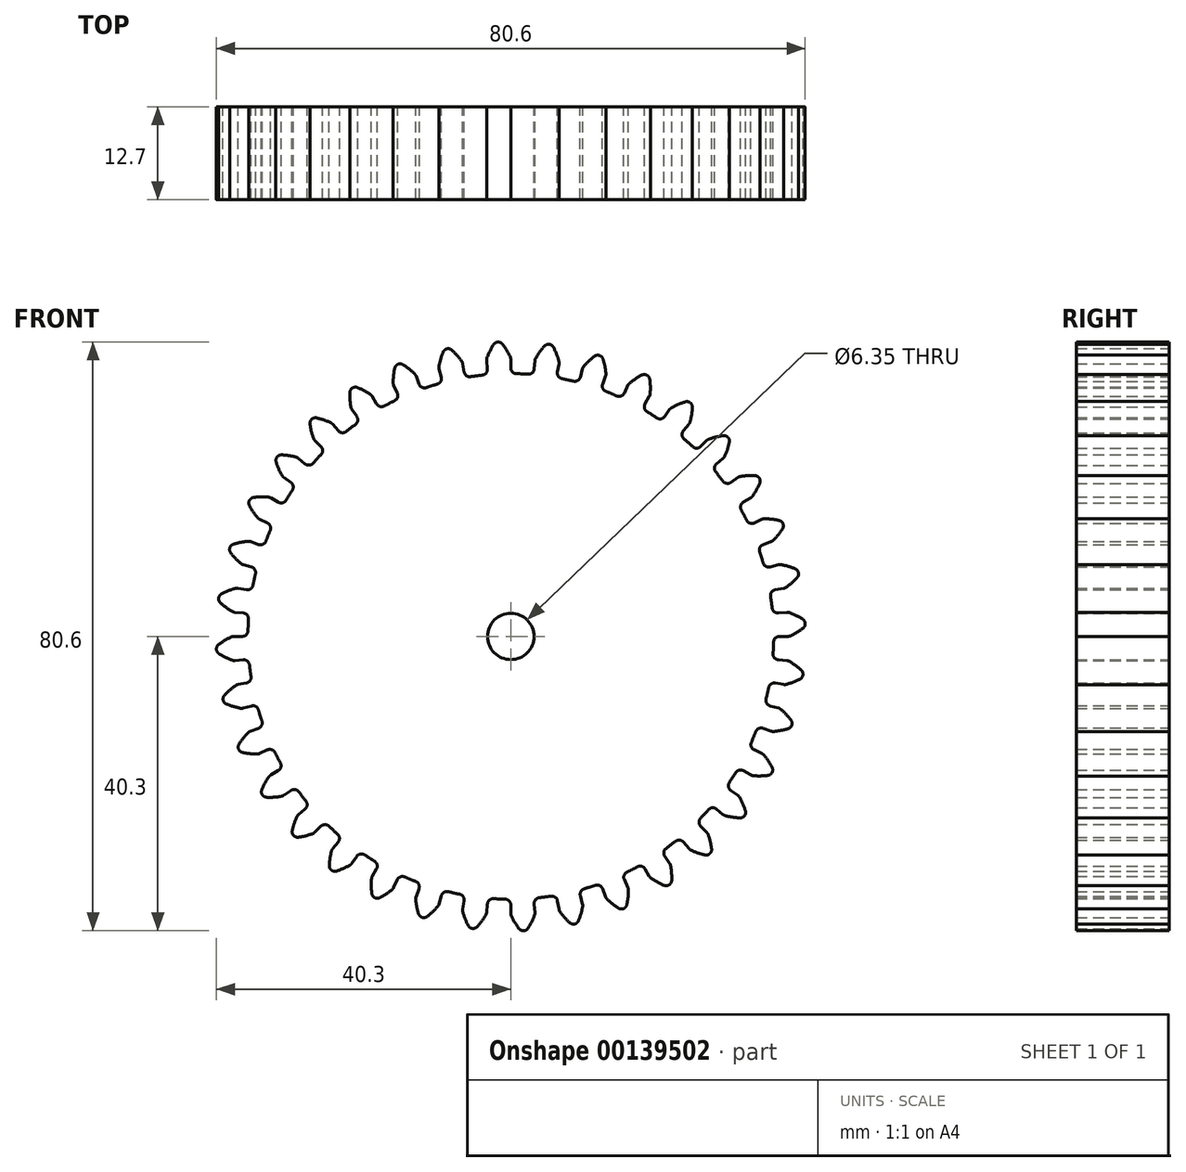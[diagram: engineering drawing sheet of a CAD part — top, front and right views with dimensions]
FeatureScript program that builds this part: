
annotation { "Feature Type Name" : "Feature", "Feature Type Description" : "" }
export const myFeature = defineFeature(function(context is Context, id is Id, definition is map)
    precondition{}
    {
        {
            var Q0;
            Q0=qCreatedBy(makeId("Front.planeOp"),FACE);
            var sketch = newSketch(context, id + "F0", { "sketchPlane" : qUnion([Q0])});
            skArc(sketch, "E0", {"start": v(-3.9, 35.77) * mm, "mid": v(-4.7, 35.67) * mm, "end": v(-5.48, 35.56) * mm});
            skArc(sketch, "E1.trimOffspring", {"start": v(-0.07, 38.26) * mm, "mid": v(-0.55, 39.16) * mm, "end": v(-1.12, 40) * mm});
            skLineSegment(sketch, "E2", {"start": v(0, 37.93) * mm, "end": v(0, 36.76) * mm});
            skLineSegment(sketch, "E3", {"start": v(-1.76, 40.3) * mm, "end": v(-1.76, 40.3) * mm});
            skLineSegment(sketch, "E4.MirrorCS", {"start": v(-3.3, 37.78) * mm, "end": v(-3.2, 36.62) * mm});
            skArc(sketch, "E5.MirrorCS", {"start": v(-3.26, 38.12) * mm, "mid": v(-2.86, 39.06) * mm, "end": v(-2.37, 39.94) * mm});
            skPoint(sketch, "E6.visualSharp", {"position": v(-3.14, 35.84) * mm});
            skArc(sketch, "E6.filletArc", {"start": v(-3.9, 35.77) * mm, "mid": v(-3.38, 36.05) * mm, "end": v(-3.2, 36.62) * mm});
            skPoint(sketch, "E7.visualSharp", {"position": v(0, 35.98) * mm});
            skArc(sketch, "E7.filletArc", {"start": v(0, 36.76) * mm, "mid": v(0.23, 36.2) * mm, "end": v(0.78, 35.97) * mm});
            skPoint(sketch, "E8.visualSharp", {"position": v(0, 38.1) * mm});
            skArc(sketch, "E8.filletArc", {"start": v(0, 37.93) * mm, "mid": v(-0.02, 38.1) * mm, "end": v(-0.07, 38.26) * mm});
            skPoint(sketch, "E9.visualSharp", {"position": v(-3.32, 37.96) * mm});
            skArc(sketch, "E9.filletArc", {"start": v(-3.26, 38.12) * mm, "mid": v(-3.3, 37.96) * mm, "end": v(-3.3, 37.78) * mm});
            skPoint(sketch, "E10.visualSharp", {"position": v(-2.14, 40.28) * mm});
            skArc(sketch, "E10.filletArc", {"start": v(-1.76, 40.3) * mm, "mid": v(-2.1, 40.2) * mm, "end": v(-2.37, 39.94) * mm});
            skPoint(sketch, "E11.visualSharp", {"position": v(-1.37, 40.31) * mm});
            skArc(sketch, "E11.filletArc", {"start": v(-1.12, 40) * mm, "mid": v(-1.4, 40.22) * mm, "end": v(-1.76, 40.3) * mm});
            skArc(sketch, "E12.1.0", {"start": v(-10.06, 34.54) * mm, "mid": v(-9.6, 34.92) * mm, "end": v(-9.52, 35.51) * mm});
            skLineSegment(sketch, "E12.1.1", {"start": v(-9.82, 36.64) * mm, "end": v(-9.52, 35.51) * mm});
            skArc(sketch, "E12.1.2", {"start": v(-9.83, 36.98) * mm, "mid": v(-9.84, 36.8) * mm, "end": v(-9.82, 36.64) * mm});
            skArc(sketch, "E12.1.3", {"start": v(-9.83, 36.98) * mm, "mid": v(-9.6, 37.97) * mm, "end": v(-9.27, 38.92) * mm});
            skArc(sketch, "E12.1.4", {"start": v(-8.73, 39.38) * mm, "mid": v(-9.05, 39.22) * mm, "end": v(-9.27, 38.92) * mm});
            skArc(sketch, "E12.1.5", {"start": v(-8.05, 39.2) * mm, "mid": v(-8.37, 39.37) * mm, "end": v(-8.73, 39.38) * mm});
            skArc(sketch, "E12.1.6", {"start": v(-6.72, 37.67) * mm, "mid": v(-7.34, 38.47) * mm, "end": v(-8.05, 39.2) * mm});
            skArc(sketch, "E12.1.7", {"start": v(-6.59, 37.35) * mm, "mid": v(-6.63, 37.52) * mm, "end": v(-6.72, 37.67) * mm});
            skLineSegment(sketch, "E12.1.8", {"start": v(-6.59, 37.35) * mm, "end": v(-6.38, 36.2) * mm});
            skArc(sketch, "E12.1.9", {"start": v(-6.38, 36.2) * mm, "mid": v(-6.06, 35.7) * mm, "end": v(-5.48, 35.56) * mm});
            skArc(sketch, "E12.2.0", {"start": v(-15.9, 32.27) * mm, "mid": v(-15.5, 32.72) * mm, "end": v(-15.54, 33.32) * mm});
            skLineSegment(sketch, "E12.2.1", {"start": v(-16.03, 34.37) * mm, "end": v(-15.54, 33.32) * mm});
            skArc(sketch, "E12.2.2", {"start": v(-16.1, 34.71) * mm, "mid": v(-16.08, 34.54) * mm, "end": v(-16.03, 34.37) * mm});
            skArc(sketch, "E12.2.3", {"start": v(-16.1, 34.71) * mm, "mid": v(-16.05, 35.72) * mm, "end": v(-15.89, 36.72) * mm});
            skArc(sketch, "E12.2.4", {"start": v(-15.43, 37.26) * mm, "mid": v(-15.73, 37.05) * mm, "end": v(-15.89, 36.72) * mm});
            skArc(sketch, "E12.2.5", {"start": v(-14.73, 37.2) * mm, "mid": v(-15.08, 37.32) * mm, "end": v(-15.44, 37.26) * mm});
            skArc(sketch, "E12.2.6", {"start": v(-13.16, 35.93) * mm, "mid": v(-13.91, 36.6) * mm, "end": v(-14.73, 37.2) * mm});
            skArc(sketch, "E12.2.7", {"start": v(-12.97, 35.64) * mm, "mid": v(-13.05, 35.8) * mm, "end": v(-13.16, 35.93) * mm});
            skLineSegment(sketch, "E12.2.8", {"start": v(-12.97, 35.64) * mm, "end": v(-12.57, 34.55) * mm});
            skArc(sketch, "E12.2.9", {"start": v(-12.57, 34.55) * mm, "mid": v(-12.17, 34.1) * mm, "end": v(-11.57, 34.07) * mm});
            skArc(sketch, "E12.3.0", {"start": v(-21.27, 29.02) * mm, "mid": v(-20.95, 29.53) * mm, "end": v(-21.09, 30.12) * mm});
            skLineSegment(sketch, "E12.3.1", {"start": v(-21.75, 31.07) * mm, "end": v(-21.09, 30.12) * mm});
            skArc(sketch, "E12.3.2", {"start": v(-21.89, 31.39) * mm, "mid": v(-21.84, 31.22) * mm, "end": v(-21.75, 31.07) * mm});
            skArc(sketch, "E12.3.3", {"start": v(-21.89, 31.39) * mm, "mid": v(-22, 32.4) * mm, "end": v(-22.02, 33.4) * mm});
            skArc(sketch, "E12.3.4", {"start": v(-21.67, 34.02) * mm, "mid": v(-21.92, 33.76) * mm, "end": v(-22.02, 33.4) * mm});
            skArc(sketch, "E12.3.5", {"start": v(-20.97, 34.08) * mm, "mid": v(-21.33, 34.13) * mm, "end": v(-21.67, 34.02) * mm});
            skArc(sketch, "E12.3.6", {"start": v(-19.2, 33.1) * mm, "mid": v(-20.06, 33.64) * mm, "end": v(-20.97, 34.08) * mm});
            skArc(sketch, "E12.3.7", {"start": v(-18.96, 32.85) * mm, "mid": v(-19.07, 32.99) * mm, "end": v(-19.2, 33.1) * mm});
            skLineSegment(sketch, "E12.3.8", {"start": v(-18.96, 32.85) * mm, "end": v(-18.38, 31.84) * mm});
            skArc(sketch, "E12.3.9", {"start": v(-18.38, 31.84) * mm, "mid": v(-17.9, 31.47) * mm, "end": v(-17.31, 31.54) * mm});
            skArc(sketch, "E12.4.0", {"start": v(-25.98, 24.89) * mm, "mid": v(-25.76, 25.44) * mm, "end": v(-26, 26) * mm});
            skLineSegment(sketch, "E12.4.1", {"start": v(-26.82, 26.82) * mm, "end": v(-26, 26) * mm});
            skArc(sketch, "E12.4.2", {"start": v(-27, 27.1) * mm, "mid": v(-26.93, 26.95) * mm, "end": v(-26.82, 26.82) * mm});
            skArc(sketch, "E12.4.3", {"start": v(-27, 27.1) * mm, "mid": v(-27.3, 28.08) * mm, "end": v(-27.49, 29.07) * mm});
            skArc(sketch, "E12.4.4", {"start": v(-27.25, 29.74) * mm, "mid": v(-27.45, 29.44) * mm, "end": v(-27.49, 29.07) * mm});
            skArc(sketch, "E12.4.5", {"start": v(-26.57, 29.92) * mm, "mid": v(-26.93, 29.9) * mm, "end": v(-27.25, 29.74) * mm});
            skArc(sketch, "E12.4.6", {"start": v(-24.65, 29.26) * mm, "mid": v(-25.6, 29.64) * mm, "end": v(-26.57, 29.92) * mm});
            skArc(sketch, "E12.4.7", {"start": v(-24.38, 29.05) * mm, "mid": v(-24.5, 29.17) * mm, "end": v(-24.65, 29.26) * mm});
            skLineSegment(sketch, "E12.4.8", {"start": v(-24.38, 29.05) * mm, "end": v(-23.63, 28.16) * mm});
            skArc(sketch, "E12.4.9", {"start": v(-23.63, 28.16) * mm, "mid": v(-23.1, 27.88) * mm, "end": v(-22.53, 28.05) * mm});
            skArc(sketch, "E12.5.0", {"start": v(-29.91, 20) * mm, "mid": v(-29.8, 20.58) * mm, "end": v(-30.12, 21.09) * mm});
            skLineSegment(sketch, "E12.5.1", {"start": v(-31.07, 21.75) * mm, "end": v(-30.12, 21.09) * mm});
            skArc(sketch, "E12.5.2", {"start": v(-31.3, 22) * mm, "mid": v(-31.2, 21.87) * mm, "end": v(-31.07, 21.75) * mm});
            skArc(sketch, "E12.5.3", {"start": v(-31.3, 22) * mm, "mid": v(-31.76, 22.91) * mm, "end": v(-32.12, 23.86) * mm});
            skArc(sketch, "E12.5.4", {"start": v(-32, 24.56) * mm, "mid": v(-32.14, 24.22) * mm, "end": v(-32.12, 23.86) * mm});
            skArc(sketch, "E12.5.5", {"start": v(-31.36, 24.85) * mm, "mid": v(-31.72, 24.78) * mm, "end": v(-32, 24.55) * mm});
            skArc(sketch, "E12.5.6", {"start": v(-29.36, 24.54) * mm, "mid": v(-30.35, 24.75) * mm, "end": v(-31.36, 24.85) * mm});
            skArc(sketch, "E12.5.7", {"start": v(-29.05, 24.38) * mm, "mid": v(-29.2, 24.48) * mm, "end": v(-29.36, 24.54) * mm});
            skLineSegment(sketch, "E12.5.8", {"start": v(-29.05, 24.38) * mm, "end": v(-28.16, 23.63) * mm});
            skArc(sketch, "E12.5.9", {"start": v(-28.16, 23.63) * mm, "mid": v(-27.6, 23.45) * mm, "end": v(-27.06, 23.72) * mm});
            skArc(sketch, "E12.6.0", {"start": v(-32.93, 14.5) * mm, "mid": v(-32.91, 15.1) * mm, "end": v(-33.32, 15.54) * mm});
            skLineSegment(sketch, "E12.6.1", {"start": v(-34.37, 16.03) * mm, "end": v(-33.32, 15.54) * mm});
            skArc(sketch, "E12.6.2", {"start": v(-34.65, 16.24) * mm, "mid": v(-34.52, 16.12) * mm, "end": v(-34.37, 16.03) * mm});
            skArc(sketch, "E12.6.3", {"start": v(-34.65, 16.24) * mm, "mid": v(-35.26, 17.05) * mm, "end": v(-35.77, 17.92) * mm});
            skArc(sketch, "E12.6.4", {"start": v(-35.77, 18.63) * mm, "mid": v(-35.86, 18.27) * mm, "end": v(-35.77, 17.92) * mm});
            skArc(sketch, "E12.6.5", {"start": v(-35.2, 19.03) * mm, "mid": v(-35.54, 18.9) * mm, "end": v(-35.78, 18.62) * mm});
            skArc(sketch, "E12.6.6", {"start": v(-33.17, 19.07) * mm, "mid": v(-34.19, 19.1) * mm, "end": v(-35.2, 19.03) * mm});
            skArc(sketch, "E12.6.7", {"start": v(-32.85, 18.96) * mm, "mid": v(-33, 19.03) * mm, "end": v(-33.17, 19.07) * mm});
            skLineSegment(sketch, "E12.6.8", {"start": v(-32.85, 18.96) * mm, "end": v(-31.84, 18.38) * mm});
            skArc(sketch, "E12.6.9", {"start": v(-31.84, 18.38) * mm, "mid": v(-31.24, 18.3) * mm, "end": v(-30.76, 18.66) * mm});
            skArc(sketch, "E12.7.0", {"start": v(-34.95, 8.56) * mm, "mid": v(-35.03, 9.15) * mm, "end": v(-35.51, 9.52) * mm});
            skLineSegment(sketch, "E12.7.1", {"start": v(-36.64, 9.82) * mm, "end": v(-35.51, 9.52) * mm});
            skArc(sketch, "E12.7.2", {"start": v(-36.94, 9.98) * mm, "mid": v(-36.8, 9.88) * mm, "end": v(-36.64, 9.82) * mm});
            skArc(sketch, "E12.7.3", {"start": v(-36.94, 9.98) * mm, "mid": v(-37.68, 10.67) * mm, "end": v(-38.34, 11.44) * mm});
            skArc(sketch, "E12.7.4", {"start": v(-38.47, 12.13) * mm, "mid": v(-38.49, 11.77) * mm, "end": v(-38.34, 11.44) * mm});
            skArc(sketch, "E12.7.5", {"start": v(-37.97, 12.62) * mm, "mid": v(-38.28, 12.44) * mm, "end": v(-38.47, 12.13) * mm});
            skArc(sketch, "E12.7.6", {"start": v(-35.98, 13.02) * mm, "mid": v(-36.98, 12.87) * mm, "end": v(-37.97, 12.62) * mm});
            skArc(sketch, "E12.7.7", {"start": v(-35.64, 12.97) * mm, "mid": v(-35.8, 13.01) * mm, "end": v(-35.98, 13.02) * mm});
            skLineSegment(sketch, "E12.7.8", {"start": v(-35.64, 12.97) * mm, "end": v(-34.55, 12.57) * mm});
            skArc(sketch, "E12.7.9", {"start": v(-34.55, 12.57) * mm, "mid": v(-33.95, 12.6) * mm, "end": v(-33.54, 13.03) * mm});
            skArc(sketch, "E12.8.0", {"start": v(-35.9, 2.36) * mm, "mid": v(-36.1, 2.93) * mm, "end": v(-36.62, 3.2) * mm});
            skLineSegment(sketch, "E12.8.1", {"start": v(-37.78, 3.3) * mm, "end": v(-36.62, 3.2) * mm});
            skArc(sketch, "E12.8.2", {"start": v(-38.11, 3.4) * mm, "mid": v(-37.95, 3.34) * mm, "end": v(-37.78, 3.3) * mm});
            skArc(sketch, "E12.8.3", {"start": v(-38.11, 3.4) * mm, "mid": v(-38.96, 3.96) * mm, "end": v(-39.75, 4.6) * mm});
            skArc(sketch, "E12.8.4", {"start": v(-39.99, 5.27) * mm, "mid": v(-39.95, 4.9) * mm, "end": v(-39.75, 4.6) * mm});
            skArc(sketch, "E12.8.5", {"start": v(-39.58, 5.84) * mm, "mid": v(-39.86, 5.6) * mm, "end": v(-39.99, 5.26) * mm});
            skArc(sketch, "E12.8.6", {"start": v(-37.7, 6.57) * mm, "mid": v(-38.66, 6.26) * mm, "end": v(-39.58, 5.84) * mm});
            skArc(sketch, "E12.8.7", {"start": v(-37.35, 6.59) * mm, "mid": v(-37.52, 6.6) * mm, "end": v(-37.7, 6.57) * mm});
            skLineSegment(sketch, "E12.8.8", {"start": v(-37.35, 6.59) * mm, "end": v(-36.2, 6.38) * mm});
            skArc(sketch, "E12.8.9", {"start": v(-36.2, 6.38) * mm, "mid": v(-35.62, 6.51) * mm, "end": v(-35.29, 7.01) * mm});
            skArc(sketch, "E12.9.0", {"start": v(-35.77, -3.9) * mm, "mid": v(-36.05, -3.38) * mm, "end": v(-36.62, -3.2) * mm});
            skLineSegment(sketch, "E12.9.1", {"start": v(-37.78, -3.3) * mm, "end": v(-36.62, -3.2) * mm});
            skArc(sketch, "E12.9.2", {"start": v(-38.12, -3.26) * mm, "mid": v(-37.96, -3.3) * mm, "end": v(-37.78, -3.3) * mm});
            skArc(sketch, "E12.9.3", {"start": v(-38.12, -3.26) * mm, "mid": v(-39.06, -2.86) * mm, "end": v(-39.94, -2.37) * mm});
            skArc(sketch, "E12.9.4", {"start": v(-40.3, -1.76) * mm, "mid": v(-40.2, -2.1) * mm, "end": v(-39.94, -2.37) * mm});
            skArc(sketch, "E12.9.5", {"start": v(-40, -1.12) * mm, "mid": v(-40.22, -1.4) * mm, "end": v(-40.3, -1.76) * mm});
            skArc(sketch, "E12.9.6", {"start": v(-38.26, -0.07) * mm, "mid": v(-39.16, -0.55) * mm, "end": v(-40, -1.12) * mm});
            skArc(sketch, "E12.9.7", {"start": v(-37.93, 0) * mm, "mid": v(-38.1, -0.02) * mm, "end": v(-38.26, -0.07) * mm});
            skLineSegment(sketch, "E12.9.8", {"start": v(-37.93, 0) * mm, "end": v(-36.76, 0) * mm});
            skArc(sketch, "E12.9.9", {"start": v(-36.76, 0) * mm, "mid": v(-36.2, 0.23) * mm, "end": v(-35.97, 0.78) * mm});
            skArc(sketch, "E12.10.0", {"start": v(-34.54, -10.06) * mm, "mid": v(-34.92, -9.6) * mm, "end": v(-35.51, -9.52) * mm});
            skLineSegment(sketch, "E12.10.1", {"start": v(-36.64, -9.82) * mm, "end": v(-35.51, -9.52) * mm});
            skArc(sketch, "E12.10.2", {"start": v(-36.98, -9.83) * mm, "mid": v(-36.8, -9.84) * mm, "end": v(-36.64, -9.82) * mm});
            skArc(sketch, "E12.10.3", {"start": v(-36.98, -9.83) * mm, "mid": v(-37.97, -9.6) * mm, "end": v(-38.92, -9.27) * mm});
            skArc(sketch, "E12.10.4", {"start": v(-39.38, -8.73) * mm, "mid": v(-39.22, -9.05) * mm, "end": v(-38.92, -9.27) * mm});
            skArc(sketch, "E12.10.5", {"start": v(-39.2, -8.05) * mm, "mid": v(-39.37, -8.37) * mm, "end": v(-39.38, -8.73) * mm});
            skArc(sketch, "E12.10.6", {"start": v(-37.67, -6.72) * mm, "mid": v(-38.47, -7.34) * mm, "end": v(-39.2, -8.05) * mm});
            skArc(sketch, "E12.10.7", {"start": v(-37.35, -6.59) * mm, "mid": v(-37.52, -6.63) * mm, "end": v(-37.67, -6.72) * mm});
            skLineSegment(sketch, "E12.10.8", {"start": v(-37.35, -6.59) * mm, "end": v(-36.2, -6.38) * mm});
            skArc(sketch, "E12.10.9", {"start": v(-36.2, -6.38) * mm, "mid": v(-35.7, -6.06) * mm, "end": v(-35.56, -5.48) * mm});
            skArc(sketch, "E12.11.0", {"start": v(-32.27, -15.9) * mm, "mid": v(-32.72, -15.5) * mm, "end": v(-33.32, -15.54) * mm});
            skLineSegment(sketch, "E12.11.1", {"start": v(-34.37, -16.03) * mm, "end": v(-33.32, -15.54) * mm});
            skArc(sketch, "E12.11.2", {"start": v(-34.71, -16.1) * mm, "mid": v(-34.54, -16.08) * mm, "end": v(-34.37, -16.03) * mm});
            skArc(sketch, "E12.11.3", {"start": v(-34.71, -16.1) * mm, "mid": v(-35.72, -16.05) * mm, "end": v(-36.72, -15.89) * mm});
            skArc(sketch, "E12.11.4", {"start": v(-37.26, -15.43) * mm, "mid": v(-37.05, -15.73) * mm, "end": v(-36.72, -15.89) * mm});
            skArc(sketch, "E12.11.5", {"start": v(-37.2, -14.73) * mm, "mid": v(-37.32, -15.08) * mm, "end": v(-37.26, -15.44) * mm});
            skArc(sketch, "E12.11.6", {"start": v(-35.93, -13.16) * mm, "mid": v(-36.6, -13.91) * mm, "end": v(-37.2, -14.73) * mm});
            skArc(sketch, "E12.11.7", {"start": v(-35.64, -12.97) * mm, "mid": v(-35.8, -13.05) * mm, "end": v(-35.93, -13.16) * mm});
            skLineSegment(sketch, "E12.11.8", {"start": v(-35.64, -12.97) * mm, "end": v(-34.55, -12.57) * mm});
            skArc(sketch, "E12.11.9", {"start": v(-34.55, -12.57) * mm, "mid": v(-34.1, -12.17) * mm, "end": v(-34.07, -11.57) * mm});
            skArc(sketch, "E12.12.0", {"start": v(-29.02, -21.27) * mm, "mid": v(-29.53, -20.95) * mm, "end": v(-30.12, -21.09) * mm});
            skLineSegment(sketch, "E12.12.1", {"start": v(-31.07, -21.75) * mm, "end": v(-30.12, -21.09) * mm});
            skArc(sketch, "E12.12.2", {"start": v(-31.39, -21.89) * mm, "mid": v(-31.22, -21.84) * mm, "end": v(-31.07, -21.75) * mm});
            skArc(sketch, "E12.12.3", {"start": v(-31.39, -21.89) * mm, "mid": v(-32.4, -22) * mm, "end": v(-33.4, -22.02) * mm});
            skArc(sketch, "E12.12.4", {"start": v(-34.02, -21.67) * mm, "mid": v(-33.76, -21.92) * mm, "end": v(-33.4, -22.02) * mm});
            skArc(sketch, "E12.12.5", {"start": v(-34.08, -20.97) * mm, "mid": v(-34.13, -21.33) * mm, "end": v(-34.02, -21.67) * mm});
            skArc(sketch, "E12.12.6", {"start": v(-33.1, -19.2) * mm, "mid": v(-33.64, -20.06) * mm, "end": v(-34.08, -20.97) * mm});
            skArc(sketch, "E12.12.7", {"start": v(-32.85, -18.96) * mm, "mid": v(-32.99, -19.07) * mm, "end": v(-33.1, -19.2) * mm});
            skLineSegment(sketch, "E12.12.8", {"start": v(-32.85, -18.96) * mm, "end": v(-31.84, -18.38) * mm});
            skArc(sketch, "E12.12.9", {"start": v(-31.84, -18.38) * mm, "mid": v(-31.47, -17.9) * mm, "end": v(-31.54, -17.31) * mm});
            skArc(sketch, "E12.13.0", {"start": v(-24.89, -25.98) * mm, "mid": v(-25.44, -25.76) * mm, "end": v(-26, -26) * mm});
            skLineSegment(sketch, "E12.13.1", {"start": v(-26.82, -26.82) * mm, "end": v(-26, -26) * mm});
            skArc(sketch, "E12.13.2", {"start": v(-27.1, -27) * mm, "mid": v(-26.95, -26.93) * mm, "end": v(-26.82, -26.82) * mm});
            skArc(sketch, "E12.13.3", {"start": v(-27.1, -27) * mm, "mid": v(-28.08, -27.3) * mm, "end": v(-29.07, -27.49) * mm});
            skArc(sketch, "E12.13.4", {"start": v(-29.74, -27.25) * mm, "mid": v(-29.44, -27.45) * mm, "end": v(-29.07, -27.49) * mm});
            skArc(sketch, "E12.13.5", {"start": v(-29.92, -26.57) * mm, "mid": v(-29.9, -26.93) * mm, "end": v(-29.74, -27.25) * mm});
            skArc(sketch, "E12.13.6", {"start": v(-29.26, -24.65) * mm, "mid": v(-29.64, -25.6) * mm, "end": v(-29.92, -26.57) * mm});
            skArc(sketch, "E12.13.7", {"start": v(-29.05, -24.38) * mm, "mid": v(-29.17, -24.5) * mm, "end": v(-29.26, -24.65) * mm});
            skLineSegment(sketch, "E12.13.8", {"start": v(-29.05, -24.38) * mm, "end": v(-28.16, -23.63) * mm});
            skArc(sketch, "E12.13.9", {"start": v(-28.16, -23.63) * mm, "mid": v(-27.88, -23.1) * mm, "end": v(-28.05, -22.53) * mm});
            skArc(sketch, "E12.14.0", {"start": v(-20, -29.91) * mm, "mid": v(-20.58, -29.8) * mm, "end": v(-21.09, -30.12) * mm});
            skLineSegment(sketch, "E12.14.1", {"start": v(-21.75, -31.07) * mm, "end": v(-21.09, -30.12) * mm});
            skArc(sketch, "E12.14.2", {"start": v(-22, -31.3) * mm, "mid": v(-21.87, -31.2) * mm, "end": v(-21.75, -31.07) * mm});
            skArc(sketch, "E12.14.3", {"start": v(-22, -31.3) * mm, "mid": v(-22.91, -31.76) * mm, "end": v(-23.86, -32.12) * mm});
            skArc(sketch, "E12.14.4", {"start": v(-24.56, -32) * mm, "mid": v(-24.22, -32.14) * mm, "end": v(-23.86, -32.12) * mm});
            skArc(sketch, "E12.14.5", {"start": v(-24.85, -31.36) * mm, "mid": v(-24.78, -31.72) * mm, "end": v(-24.55, -32) * mm});
            skArc(sketch, "E12.14.6", {"start": v(-24.54, -29.36) * mm, "mid": v(-24.75, -30.35) * mm, "end": v(-24.85, -31.36) * mm});
            skArc(sketch, "E12.14.7", {"start": v(-24.38, -29.05) * mm, "mid": v(-24.48, -29.2) * mm, "end": v(-24.54, -29.36) * mm});
            skLineSegment(sketch, "E12.14.8", {"start": v(-24.38, -29.05) * mm, "end": v(-23.63, -28.16) * mm});
            skArc(sketch, "E12.14.9", {"start": v(-23.63, -28.16) * mm, "mid": v(-23.45, -27.6) * mm, "end": v(-23.72, -27.06) * mm});
            skArc(sketch, "E12.15.0", {"start": v(-14.5, -32.93) * mm, "mid": v(-15.1, -32.91) * mm, "end": v(-15.54, -33.32) * mm});
            skLineSegment(sketch, "E12.15.1", {"start": v(-16.03, -34.37) * mm, "end": v(-15.54, -33.32) * mm});
            skArc(sketch, "E12.15.2", {"start": v(-16.24, -34.65) * mm, "mid": v(-16.12, -34.52) * mm, "end": v(-16.03, -34.37) * mm});
            skArc(sketch, "E12.15.3", {"start": v(-16.24, -34.65) * mm, "mid": v(-17.05, -35.26) * mm, "end": v(-17.92, -35.77) * mm});
            skArc(sketch, "E12.15.4", {"start": v(-18.63, -35.77) * mm, "mid": v(-18.27, -35.86) * mm, "end": v(-17.92, -35.77) * mm});
            skArc(sketch, "E12.15.5", {"start": v(-19.03, -35.2) * mm, "mid": v(-18.9, -35.54) * mm, "end": v(-18.62, -35.78) * mm});
            skArc(sketch, "E12.15.6", {"start": v(-19.07, -33.17) * mm, "mid": v(-19.1, -34.19) * mm, "end": v(-19.03, -35.2) * mm});
            skArc(sketch, "E12.15.7", {"start": v(-18.96, -32.85) * mm, "mid": v(-19.03, -33) * mm, "end": v(-19.07, -33.17) * mm});
            skLineSegment(sketch, "E12.15.8", {"start": v(-18.96, -32.85) * mm, "end": v(-18.38, -31.84) * mm});
            skArc(sketch, "E12.15.9", {"start": v(-18.38, -31.84) * mm, "mid": v(-18.3, -31.24) * mm, "end": v(-18.66, -30.76) * mm});
            skArc(sketch, "E12.16.0", {"start": v(-8.56, -34.95) * mm, "mid": v(-9.15, -35.03) * mm, "end": v(-9.52, -35.51) * mm});
            skLineSegment(sketch, "E12.16.1", {"start": v(-9.82, -36.64) * mm, "end": v(-9.52, -35.51) * mm});
            skArc(sketch, "E12.16.2", {"start": v(-9.98, -36.94) * mm, "mid": v(-9.88, -36.8) * mm, "end": v(-9.82, -36.64) * mm});
            skArc(sketch, "E12.16.3", {"start": v(-9.98, -36.94) * mm, "mid": v(-10.67, -37.68) * mm, "end": v(-11.44, -38.34) * mm});
            skArc(sketch, "E12.16.4", {"start": v(-12.13, -38.47) * mm, "mid": v(-11.77, -38.49) * mm, "end": v(-11.44, -38.34) * mm});
            skArc(sketch, "E12.16.5", {"start": v(-12.62, -37.97) * mm, "mid": v(-12.44, -38.28) * mm, "end": v(-12.13, -38.47) * mm});
            skArc(sketch, "E12.16.6", {"start": v(-13.02, -35.98) * mm, "mid": v(-12.87, -36.98) * mm, "end": v(-12.62, -37.97) * mm});
            skArc(sketch, "E12.16.7", {"start": v(-12.97, -35.64) * mm, "mid": v(-13.01, -35.8) * mm, "end": v(-13.02, -35.98) * mm});
            skLineSegment(sketch, "E12.16.8", {"start": v(-12.97, -35.64) * mm, "end": v(-12.57, -34.55) * mm});
            skArc(sketch, "E12.16.9", {"start": v(-12.57, -34.55) * mm, "mid": v(-12.6, -33.95) * mm, "end": v(-13.03, -33.54) * mm});
            skArc(sketch, "E12.17.0", {"start": v(-2.36, -35.9) * mm, "mid": v(-2.93, -36.1) * mm, "end": v(-3.2, -36.62) * mm});
            skLineSegment(sketch, "E12.17.1", {"start": v(-3.3, -37.78) * mm, "end": v(-3.2, -36.62) * mm});
            skArc(sketch, "E12.17.2", {"start": v(-3.4, -38.11) * mm, "mid": v(-3.34, -37.95) * mm, "end": v(-3.3, -37.78) * mm});
            skArc(sketch, "E12.17.3", {"start": v(-3.4, -38.11) * mm, "mid": v(-3.96, -38.96) * mm, "end": v(-4.6, -39.75) * mm});
            skArc(sketch, "E12.17.4", {"start": v(-5.27, -39.99) * mm, "mid": v(-4.9, -39.95) * mm, "end": v(-4.6, -39.75) * mm});
            skArc(sketch, "E12.17.5", {"start": v(-5.84, -39.58) * mm, "mid": v(-5.6, -39.86) * mm, "end": v(-5.26, -39.99) * mm});
            skArc(sketch, "E12.17.6", {"start": v(-6.57, -37.7) * mm, "mid": v(-6.26, -38.66) * mm, "end": v(-5.84, -39.58) * mm});
            skArc(sketch, "E12.17.7", {"start": v(-6.59, -37.35) * mm, "mid": v(-6.6, -37.52) * mm, "end": v(-6.57, -37.7) * mm});
            skLineSegment(sketch, "E12.17.8", {"start": v(-6.59, -37.35) * mm, "end": v(-6.38, -36.2) * mm});
            skArc(sketch, "E12.17.9", {"start": v(-6.38, -36.2) * mm, "mid": v(-6.51, -35.62) * mm, "end": v(-7.01, -35.29) * mm});
            skArc(sketch, "E12.18.0", {"start": v(3.9, -35.77) * mm, "mid": v(3.38, -36.05) * mm, "end": v(3.2, -36.62) * mm});
            skLineSegment(sketch, "E12.18.1", {"start": v(3.3, -37.78) * mm, "end": v(3.2, -36.62) * mm});
            skArc(sketch, "E12.18.2", {"start": v(3.26, -38.12) * mm, "mid": v(3.3, -37.96) * mm, "end": v(3.3, -37.78) * mm});
            skArc(sketch, "E12.18.3", {"start": v(3.26, -38.12) * mm, "mid": v(2.86, -39.06) * mm, "end": v(2.37, -39.94) * mm});
            skArc(sketch, "E12.18.4", {"start": v(1.76, -40.3) * mm, "mid": v(2.1, -40.2) * mm, "end": v(2.37, -39.94) * mm});
            skArc(sketch, "E12.18.5", {"start": v(1.12, -40) * mm, "mid": v(1.4, -40.22) * mm, "end": v(1.76, -40.3) * mm});
            skArc(sketch, "E12.18.6", {"start": v(0.07, -38.26) * mm, "mid": v(0.55, -39.16) * mm, "end": v(1.12, -40) * mm});
            skArc(sketch, "E12.18.7", {"start": v(0, -37.93) * mm, "mid": v(0.02, -38.1) * mm, "end": v(0.07, -38.26) * mm});
            skLineSegment(sketch, "E12.18.8", {"start": v(0, -37.93) * mm, "end": v(0, -36.76) * mm});
            skArc(sketch, "E12.18.9", {"start": v(0, -36.76) * mm, "mid": v(-0.23, -36.2) * mm, "end": v(-0.78, -35.97) * mm});
            skArc(sketch, "E12.19.0", {"start": v(10.06, -34.54) * mm, "mid": v(9.6, -34.92) * mm, "end": v(9.52, -35.51) * mm});
            skLineSegment(sketch, "E12.19.1", {"start": v(9.82, -36.64) * mm, "end": v(9.52, -35.51) * mm});
            skArc(sketch, "E12.19.2", {"start": v(9.83, -36.98) * mm, "mid": v(9.84, -36.8) * mm, "end": v(9.82, -36.64) * mm});
            skArc(sketch, "E12.19.3", {"start": v(9.83, -36.98) * mm, "mid": v(9.6, -37.97) * mm, "end": v(9.27, -38.92) * mm});
            skArc(sketch, "E12.19.4", {"start": v(8.73, -39.38) * mm, "mid": v(9.05, -39.22) * mm, "end": v(9.27, -38.92) * mm});
            skArc(sketch, "E12.19.5", {"start": v(8.05, -39.2) * mm, "mid": v(8.37, -39.37) * mm, "end": v(8.73, -39.38) * mm});
            skArc(sketch, "E12.19.6", {"start": v(6.72, -37.67) * mm, "mid": v(7.34, -38.47) * mm, "end": v(8.05, -39.2) * mm});
            skArc(sketch, "E12.19.7", {"start": v(6.59, -37.35) * mm, "mid": v(6.63, -37.52) * mm, "end": v(6.72, -37.67) * mm});
            skLineSegment(sketch, "E12.19.8", {"start": v(6.59, -37.35) * mm, "end": v(6.38, -36.2) * mm});
            skArc(sketch, "E12.19.9", {"start": v(6.38, -36.2) * mm, "mid": v(6.06, -35.7) * mm, "end": v(5.48, -35.56) * mm});
            skArc(sketch, "E12.20.0", {"start": v(15.9, -32.27) * mm, "mid": v(15.5, -32.72) * mm, "end": v(15.54, -33.32) * mm});
            skLineSegment(sketch, "E12.20.1", {"start": v(16.03, -34.37) * mm, "end": v(15.54, -33.32) * mm});
            skArc(sketch, "E12.20.2", {"start": v(16.1, -34.71) * mm, "mid": v(16.08, -34.54) * mm, "end": v(16.03, -34.37) * mm});
            skArc(sketch, "E12.20.3", {"start": v(16.1, -34.71) * mm, "mid": v(16.05, -35.72) * mm, "end": v(15.89, -36.72) * mm});
            skArc(sketch, "E12.20.4", {"start": v(15.43, -37.26) * mm, "mid": v(15.73, -37.05) * mm, "end": v(15.89, -36.72) * mm});
            skArc(sketch, "E12.20.5", {"start": v(14.73, -37.2) * mm, "mid": v(15.08, -37.32) * mm, "end": v(15.44, -37.26) * mm});
            skArc(sketch, "E12.20.6", {"start": v(13.16, -35.93) * mm, "mid": v(13.91, -36.6) * mm, "end": v(14.73, -37.2) * mm});
            skArc(sketch, "E12.20.7", {"start": v(12.97, -35.64) * mm, "mid": v(13.05, -35.8) * mm, "end": v(13.16, -35.93) * mm});
            skLineSegment(sketch, "E12.20.8", {"start": v(12.97, -35.64) * mm, "end": v(12.57, -34.55) * mm});
            skArc(sketch, "E12.20.9", {"start": v(12.57, -34.55) * mm, "mid": v(12.17, -34.1) * mm, "end": v(11.57, -34.07) * mm});
            skArc(sketch, "E12.21.0", {"start": v(21.27, -29.02) * mm, "mid": v(20.95, -29.53) * mm, "end": v(21.09, -30.12) * mm});
            skLineSegment(sketch, "E12.21.1", {"start": v(21.75, -31.07) * mm, "end": v(21.09, -30.12) * mm});
            skArc(sketch, "E12.21.2", {"start": v(21.89, -31.39) * mm, "mid": v(21.84, -31.22) * mm, "end": v(21.75, -31.07) * mm});
            skArc(sketch, "E12.21.3", {"start": v(21.89, -31.39) * mm, "mid": v(22, -32.4) * mm, "end": v(22.02, -33.4) * mm});
            skArc(sketch, "E12.21.4", {"start": v(21.67, -34.02) * mm, "mid": v(21.92, -33.76) * mm, "end": v(22.02, -33.4) * mm});
            skArc(sketch, "E12.21.5", {"start": v(20.97, -34.08) * mm, "mid": v(21.33, -34.13) * mm, "end": v(21.67, -34.02) * mm});
            skArc(sketch, "E12.21.6", {"start": v(19.2, -33.1) * mm, "mid": v(20.06, -33.64) * mm, "end": v(20.97, -34.08) * mm});
            skArc(sketch, "E12.21.7", {"start": v(18.96, -32.85) * mm, "mid": v(19.07, -32.99) * mm, "end": v(19.2, -33.1) * mm});
            skLineSegment(sketch, "E12.21.8", {"start": v(18.96, -32.85) * mm, "end": v(18.38, -31.84) * mm});
            skArc(sketch, "E12.21.9", {"start": v(18.38, -31.84) * mm, "mid": v(17.9, -31.47) * mm, "end": v(17.31, -31.54) * mm});
            skArc(sketch, "E12.22.0", {"start": v(25.98, -24.89) * mm, "mid": v(25.76, -25.44) * mm, "end": v(26, -26) * mm});
            skLineSegment(sketch, "E12.22.1", {"start": v(26.82, -26.82) * mm, "end": v(26, -26) * mm});
            skArc(sketch, "E12.22.2", {"start": v(27, -27.1) * mm, "mid": v(26.93, -26.95) * mm, "end": v(26.82, -26.82) * mm});
            skArc(sketch, "E12.22.3", {"start": v(27, -27.1) * mm, "mid": v(27.3, -28.08) * mm, "end": v(27.49, -29.07) * mm});
            skArc(sketch, "E12.22.4", {"start": v(27.25, -29.74) * mm, "mid": v(27.45, -29.44) * mm, "end": v(27.49, -29.07) * mm});
            skArc(sketch, "E12.22.5", {"start": v(26.57, -29.92) * mm, "mid": v(26.93, -29.9) * mm, "end": v(27.25, -29.74) * mm});
            skArc(sketch, "E12.22.6", {"start": v(24.65, -29.26) * mm, "mid": v(25.6, -29.64) * mm, "end": v(26.57, -29.92) * mm});
            skArc(sketch, "E12.22.7", {"start": v(24.38, -29.05) * mm, "mid": v(24.5, -29.17) * mm, "end": v(24.65, -29.26) * mm});
            skLineSegment(sketch, "E12.22.8", {"start": v(24.38, -29.05) * mm, "end": v(23.63, -28.16) * mm});
            skArc(sketch, "E12.22.9", {"start": v(23.63, -28.16) * mm, "mid": v(23.1, -27.88) * mm, "end": v(22.53, -28.05) * mm});
            skArc(sketch, "E12.23.0", {"start": v(29.91, -20) * mm, "mid": v(29.8, -20.58) * mm, "end": v(30.12, -21.09) * mm});
            skLineSegment(sketch, "E12.23.1", {"start": v(31.07, -21.75) * mm, "end": v(30.12, -21.09) * mm});
            skArc(sketch, "E12.23.2", {"start": v(31.3, -22) * mm, "mid": v(31.2, -21.87) * mm, "end": v(31.07, -21.75) * mm});
            skArc(sketch, "E12.23.3", {"start": v(31.3, -22) * mm, "mid": v(31.76, -22.91) * mm, "end": v(32.12, -23.86) * mm});
            skArc(sketch, "E12.23.4", {"start": v(32, -24.56) * mm, "mid": v(32.14, -24.22) * mm, "end": v(32.12, -23.86) * mm});
            skArc(sketch, "E12.23.5", {"start": v(31.36, -24.85) * mm, "mid": v(31.72, -24.78) * mm, "end": v(32, -24.55) * mm});
            skArc(sketch, "E12.23.6", {"start": v(29.36, -24.54) * mm, "mid": v(30.35, -24.75) * mm, "end": v(31.36, -24.85) * mm});
            skArc(sketch, "E12.23.7", {"start": v(29.05, -24.38) * mm, "mid": v(29.2, -24.48) * mm, "end": v(29.36, -24.54) * mm});
            skLineSegment(sketch, "E12.23.8", {"start": v(29.05, -24.38) * mm, "end": v(28.16, -23.63) * mm});
            skArc(sketch, "E12.23.9", {"start": v(28.16, -23.63) * mm, "mid": v(27.6, -23.45) * mm, "end": v(27.06, -23.72) * mm});
            skArc(sketch, "E12.24.0", {"start": v(32.93, -14.5) * mm, "mid": v(32.91, -15.1) * mm, "end": v(33.32, -15.54) * mm});
            skLineSegment(sketch, "E12.24.1", {"start": v(34.37, -16.03) * mm, "end": v(33.32, -15.54) * mm});
            skArc(sketch, "E12.24.2", {"start": v(34.65, -16.24) * mm, "mid": v(34.52, -16.12) * mm, "end": v(34.37, -16.03) * mm});
            skArc(sketch, "E12.24.3", {"start": v(34.65, -16.24) * mm, "mid": v(35.26, -17.05) * mm, "end": v(35.77, -17.92) * mm});
            skArc(sketch, "E12.24.4", {"start": v(35.77, -18.63) * mm, "mid": v(35.86, -18.27) * mm, "end": v(35.77, -17.92) * mm});
            skArc(sketch, "E12.24.5", {"start": v(35.2, -19.03) * mm, "mid": v(35.54, -18.9) * mm, "end": v(35.78, -18.62) * mm});
            skArc(sketch, "E12.24.6", {"start": v(33.17, -19.07) * mm, "mid": v(34.19, -19.1) * mm, "end": v(35.2, -19.03) * mm});
            skArc(sketch, "E12.24.7", {"start": v(32.85, -18.96) * mm, "mid": v(33, -19.03) * mm, "end": v(33.17, -19.07) * mm});
            skLineSegment(sketch, "E12.24.8", {"start": v(32.85, -18.96) * mm, "end": v(31.84, -18.38) * mm});
            skArc(sketch, "E12.24.9", {"start": v(31.84, -18.38) * mm, "mid": v(31.24, -18.3) * mm, "end": v(30.76, -18.66) * mm});
            skArc(sketch, "E12.25.0", {"start": v(34.95, -8.56) * mm, "mid": v(35.03, -9.15) * mm, "end": v(35.51, -9.52) * mm});
            skLineSegment(sketch, "E12.25.1", {"start": v(36.64, -9.82) * mm, "end": v(35.51, -9.52) * mm});
            skArc(sketch, "E12.25.2", {"start": v(36.94, -9.98) * mm, "mid": v(36.8, -9.88) * mm, "end": v(36.64, -9.82) * mm});
            skArc(sketch, "E12.25.3", {"start": v(36.94, -9.98) * mm, "mid": v(37.68, -10.67) * mm, "end": v(38.34, -11.44) * mm});
            skArc(sketch, "E12.25.4", {"start": v(38.47, -12.13) * mm, "mid": v(38.49, -11.77) * mm, "end": v(38.34, -11.44) * mm});
            skArc(sketch, "E12.25.5", {"start": v(37.97, -12.62) * mm, "mid": v(38.28, -12.44) * mm, "end": v(38.47, -12.13) * mm});
            skArc(sketch, "E12.25.6", {"start": v(35.98, -13.02) * mm, "mid": v(36.98, -12.87) * mm, "end": v(37.97, -12.62) * mm});
            skArc(sketch, "E12.25.7", {"start": v(35.64, -12.97) * mm, "mid": v(35.8, -13.01) * mm, "end": v(35.98, -13.02) * mm});
            skLineSegment(sketch, "E12.25.8", {"start": v(35.64, -12.97) * mm, "end": v(34.55, -12.57) * mm});
            skArc(sketch, "E12.25.9", {"start": v(34.55, -12.57) * mm, "mid": v(33.95, -12.6) * mm, "end": v(33.54, -13.03) * mm});
            skArc(sketch, "E12.26.0", {"start": v(35.9, -2.36) * mm, "mid": v(36.1, -2.93) * mm, "end": v(36.62, -3.2) * mm});
            skLineSegment(sketch, "E12.26.1", {"start": v(37.78, -3.3) * mm, "end": v(36.62, -3.2) * mm});
            skArc(sketch, "E12.26.2", {"start": v(38.11, -3.4) * mm, "mid": v(37.95, -3.34) * mm, "end": v(37.78, -3.3) * mm});
            skArc(sketch, "E12.26.3", {"start": v(38.11, -3.4) * mm, "mid": v(38.96, -3.96) * mm, "end": v(39.75, -4.6) * mm});
            skArc(sketch, "E12.26.4", {"start": v(39.99, -5.27) * mm, "mid": v(39.95, -4.9) * mm, "end": v(39.75, -4.6) * mm});
            skArc(sketch, "E12.26.5", {"start": v(39.58, -5.84) * mm, "mid": v(39.86, -5.6) * mm, "end": v(39.99, -5.26) * mm});
            skArc(sketch, "E12.26.6", {"start": v(37.7, -6.57) * mm, "mid": v(38.66, -6.26) * mm, "end": v(39.58, -5.84) * mm});
            skArc(sketch, "E12.26.7", {"start": v(37.35, -6.59) * mm, "mid": v(37.52, -6.6) * mm, "end": v(37.7, -6.57) * mm});
            skLineSegment(sketch, "E12.26.8", {"start": v(37.35, -6.59) * mm, "end": v(36.2, -6.38) * mm});
            skArc(sketch, "E12.26.9", {"start": v(36.2, -6.38) * mm, "mid": v(35.62, -6.51) * mm, "end": v(35.29, -7.01) * mm});
            skArc(sketch, "E12.27.0", {"start": v(35.77, 3.9) * mm, "mid": v(36.05, 3.38) * mm, "end": v(36.62, 3.2) * mm});
            skLineSegment(sketch, "E12.27.1", {"start": v(37.78, 3.3) * mm, "end": v(36.62, 3.2) * mm});
            skArc(sketch, "E12.27.2", {"start": v(38.12, 3.26) * mm, "mid": v(37.96, 3.3) * mm, "end": v(37.78, 3.3) * mm});
            skArc(sketch, "E12.27.3", {"start": v(38.12, 3.26) * mm, "mid": v(39.06, 2.86) * mm, "end": v(39.94, 2.37) * mm});
            skArc(sketch, "E12.27.4", {"start": v(40.3, 1.76) * mm, "mid": v(40.2, 2.1) * mm, "end": v(39.94, 2.37) * mm});
            skArc(sketch, "E12.27.5", {"start": v(40, 1.12) * mm, "mid": v(40.22, 1.4) * mm, "end": v(40.3, 1.76) * mm});
            skArc(sketch, "E12.27.6", {"start": v(38.26, 0.07) * mm, "mid": v(39.16, 0.55) * mm, "end": v(40, 1.12) * mm});
            skArc(sketch, "E12.27.7", {"start": v(37.93, 0) * mm, "mid": v(38.1, 0.02) * mm, "end": v(38.26, 0.07) * mm});
            skLineSegment(sketch, "E12.27.8", {"start": v(37.93, 0) * mm, "end": v(36.76, 0) * mm});
            skArc(sketch, "E12.27.9", {"start": v(36.76, 0) * mm, "mid": v(36.2, -0.23) * mm, "end": v(35.97, -0.78) * mm});
            skArc(sketch, "E12.28.0", {"start": v(34.54, 10.06) * mm, "mid": v(34.92, 9.6) * mm, "end": v(35.51, 9.52) * mm});
            skLineSegment(sketch, "E12.28.1", {"start": v(36.64, 9.82) * mm, "end": v(35.51, 9.52) * mm});
            skArc(sketch, "E12.28.2", {"start": v(36.98, 9.83) * mm, "mid": v(36.8, 9.84) * mm, "end": v(36.64, 9.82) * mm});
            skArc(sketch, "E12.28.3", {"start": v(36.98, 9.83) * mm, "mid": v(37.97, 9.6) * mm, "end": v(38.92, 9.27) * mm});
            skArc(sketch, "E12.28.4", {"start": v(39.38, 8.73) * mm, "mid": v(39.22, 9.05) * mm, "end": v(38.92, 9.27) * mm});
            skArc(sketch, "E12.28.5", {"start": v(39.2, 8.05) * mm, "mid": v(39.37, 8.37) * mm, "end": v(39.38, 8.73) * mm});
            skArc(sketch, "E12.28.6", {"start": v(37.67, 6.72) * mm, "mid": v(38.47, 7.34) * mm, "end": v(39.2, 8.05) * mm});
            skArc(sketch, "E12.28.7", {"start": v(37.35, 6.59) * mm, "mid": v(37.52, 6.63) * mm, "end": v(37.67, 6.72) * mm});
            skLineSegment(sketch, "E12.28.8", {"start": v(37.35, 6.59) * mm, "end": v(36.2, 6.38) * mm});
            skArc(sketch, "E12.28.9", {"start": v(36.2, 6.38) * mm, "mid": v(35.7, 6.06) * mm, "end": v(35.56, 5.48) * mm});
            skArc(sketch, "E12.29.0", {"start": v(32.27, 15.9) * mm, "mid": v(32.72, 15.5) * mm, "end": v(33.32, 15.54) * mm});
            skLineSegment(sketch, "E12.29.1", {"start": v(34.37, 16.03) * mm, "end": v(33.32, 15.54) * mm});
            skArc(sketch, "E12.29.2", {"start": v(34.71, 16.1) * mm, "mid": v(34.54, 16.08) * mm, "end": v(34.37, 16.03) * mm});
            skArc(sketch, "E12.29.3", {"start": v(34.71, 16.1) * mm, "mid": v(35.72, 16.05) * mm, "end": v(36.72, 15.89) * mm});
            skArc(sketch, "E12.29.4", {"start": v(37.26, 15.43) * mm, "mid": v(37.05, 15.73) * mm, "end": v(36.72, 15.89) * mm});
            skArc(sketch, "E12.29.5", {"start": v(37.2, 14.73) * mm, "mid": v(37.32, 15.08) * mm, "end": v(37.26, 15.44) * mm});
            skArc(sketch, "E12.29.6", {"start": v(35.93, 13.16) * mm, "mid": v(36.6, 13.91) * mm, "end": v(37.2, 14.73) * mm});
            skArc(sketch, "E12.29.7", {"start": v(35.64, 12.97) * mm, "mid": v(35.8, 13.05) * mm, "end": v(35.93, 13.16) * mm});
            skLineSegment(sketch, "E12.29.8", {"start": v(35.64, 12.97) * mm, "end": v(34.55, 12.57) * mm});
            skArc(sketch, "E12.29.9", {"start": v(34.55, 12.57) * mm, "mid": v(34.1, 12.17) * mm, "end": v(34.07, 11.57) * mm});
            skArc(sketch, "E12.30.0", {"start": v(29.02, 21.27) * mm, "mid": v(29.53, 20.95) * mm, "end": v(30.12, 21.09) * mm});
            skLineSegment(sketch, "E12.30.1", {"start": v(31.07, 21.75) * mm, "end": v(30.12, 21.09) * mm});
            skArc(sketch, "E12.30.2", {"start": v(31.39, 21.89) * mm, "mid": v(31.22, 21.84) * mm, "end": v(31.07, 21.75) * mm});
            skArc(sketch, "E12.30.3", {"start": v(31.39, 21.89) * mm, "mid": v(32.4, 22) * mm, "end": v(33.4, 22.02) * mm});
            skArc(sketch, "E12.30.4", {"start": v(34.02, 21.67) * mm, "mid": v(33.76, 21.92) * mm, "end": v(33.4, 22.02) * mm});
            skArc(sketch, "E12.30.5", {"start": v(34.08, 20.97) * mm, "mid": v(34.13, 21.33) * mm, "end": v(34.02, 21.67) * mm});
            skArc(sketch, "E12.30.6", {"start": v(33.1, 19.2) * mm, "mid": v(33.64, 20.06) * mm, "end": v(34.08, 20.97) * mm});
            skArc(sketch, "E12.30.7", {"start": v(32.85, 18.96) * mm, "mid": v(32.99, 19.07) * mm, "end": v(33.1, 19.2) * mm});
            skLineSegment(sketch, "E12.30.8", {"start": v(32.85, 18.96) * mm, "end": v(31.84, 18.38) * mm});
            skArc(sketch, "E12.30.9", {"start": v(31.84, 18.38) * mm, "mid": v(31.47, 17.9) * mm, "end": v(31.54, 17.31) * mm});
            skArc(sketch, "E12.31.0", {"start": v(24.89, 25.98) * mm, "mid": v(25.44, 25.76) * mm, "end": v(26, 26) * mm});
            skLineSegment(sketch, "E12.31.1", {"start": v(26.82, 26.82) * mm, "end": v(26, 26) * mm});
            skArc(sketch, "E12.31.2", {"start": v(27.1, 27) * mm, "mid": v(26.95, 26.93) * mm, "end": v(26.82, 26.82) * mm});
            skArc(sketch, "E12.31.3", {"start": v(27.1, 27) * mm, "mid": v(28.08, 27.3) * mm, "end": v(29.07, 27.49) * mm});
            skArc(sketch, "E12.31.4", {"start": v(29.74, 27.25) * mm, "mid": v(29.44, 27.45) * mm, "end": v(29.07, 27.49) * mm});
            skArc(sketch, "E12.31.5", {"start": v(29.92, 26.57) * mm, "mid": v(29.9, 26.93) * mm, "end": v(29.74, 27.25) * mm});
            skArc(sketch, "E12.31.6", {"start": v(29.26, 24.65) * mm, "mid": v(29.64, 25.6) * mm, "end": v(29.92, 26.57) * mm});
            skArc(sketch, "E12.31.7", {"start": v(29.05, 24.38) * mm, "mid": v(29.17, 24.5) * mm, "end": v(29.26, 24.65) * mm});
            skLineSegment(sketch, "E12.31.8", {"start": v(29.05, 24.38) * mm, "end": v(28.16, 23.63) * mm});
            skArc(sketch, "E12.31.9", {"start": v(28.16, 23.63) * mm, "mid": v(27.88, 23.1) * mm, "end": v(28.05, 22.53) * mm});
            skArc(sketch, "E12.32.0", {"start": v(20, 29.91) * mm, "mid": v(20.58, 29.8) * mm, "end": v(21.09, 30.12) * mm});
            skLineSegment(sketch, "E12.32.1", {"start": v(21.75, 31.07) * mm, "end": v(21.09, 30.12) * mm});
            skArc(sketch, "E12.32.2", {"start": v(22, 31.3) * mm, "mid": v(21.87, 31.2) * mm, "end": v(21.75, 31.07) * mm});
            skArc(sketch, "E12.32.3", {"start": v(22, 31.3) * mm, "mid": v(22.91, 31.76) * mm, "end": v(23.86, 32.12) * mm});
            skArc(sketch, "E12.32.4", {"start": v(24.56, 32) * mm, "mid": v(24.22, 32.14) * mm, "end": v(23.86, 32.12) * mm});
            skArc(sketch, "E12.32.5", {"start": v(24.85, 31.36) * mm, "mid": v(24.78, 31.72) * mm, "end": v(24.55, 32) * mm});
            skArc(sketch, "E12.32.6", {"start": v(24.54, 29.36) * mm, "mid": v(24.75, 30.35) * mm, "end": v(24.85, 31.36) * mm});
            skArc(sketch, "E12.32.7", {"start": v(24.38, 29.05) * mm, "mid": v(24.48, 29.2) * mm, "end": v(24.54, 29.36) * mm});
            skLineSegment(sketch, "E12.32.8", {"start": v(24.38, 29.05) * mm, "end": v(23.63, 28.16) * mm});
            skArc(sketch, "E12.32.9", {"start": v(23.63, 28.16) * mm, "mid": v(23.45, 27.6) * mm, "end": v(23.72, 27.06) * mm});
            skArc(sketch, "E12.33.0", {"start": v(14.5, 32.93) * mm, "mid": v(15.1, 32.91) * mm, "end": v(15.54, 33.32) * mm});
            skLineSegment(sketch, "E12.33.1", {"start": v(16.03, 34.37) * mm, "end": v(15.54, 33.32) * mm});
            skArc(sketch, "E12.33.2", {"start": v(16.24, 34.65) * mm, "mid": v(16.12, 34.52) * mm, "end": v(16.03, 34.37) * mm});
            skArc(sketch, "E12.33.3", {"start": v(16.24, 34.65) * mm, "mid": v(17.05, 35.26) * mm, "end": v(17.92, 35.77) * mm});
            skArc(sketch, "E12.33.4", {"start": v(18.63, 35.77) * mm, "mid": v(18.27, 35.86) * mm, "end": v(17.92, 35.77) * mm});
            skArc(sketch, "E12.33.5", {"start": v(19.03, 35.2) * mm, "mid": v(18.9, 35.54) * mm, "end": v(18.62, 35.78) * mm});
            skArc(sketch, "E12.33.6", {"start": v(19.07, 33.17) * mm, "mid": v(19.1, 34.19) * mm, "end": v(19.03, 35.2) * mm});
            skArc(sketch, "E12.33.7", {"start": v(18.96, 32.85) * mm, "mid": v(19.03, 33) * mm, "end": v(19.07, 33.17) * mm});
            skLineSegment(sketch, "E12.33.8", {"start": v(18.96, 32.85) * mm, "end": v(18.38, 31.84) * mm});
            skArc(sketch, "E12.33.9", {"start": v(18.38, 31.84) * mm, "mid": v(18.3, 31.24) * mm, "end": v(18.66, 30.76) * mm});
            skArc(sketch, "E12.34.0", {"start": v(8.56, 34.95) * mm, "mid": v(9.15, 35.03) * mm, "end": v(9.52, 35.51) * mm});
            skLineSegment(sketch, "E12.34.1", {"start": v(9.82, 36.64) * mm, "end": v(9.52, 35.51) * mm});
            skArc(sketch, "E12.34.2", {"start": v(9.98, 36.94) * mm, "mid": v(9.88, 36.8) * mm, "end": v(9.82, 36.64) * mm});
            skArc(sketch, "E12.34.3", {"start": v(9.98, 36.94) * mm, "mid": v(10.67, 37.68) * mm, "end": v(11.44, 38.34) * mm});
            skArc(sketch, "E12.34.4", {"start": v(12.13, 38.47) * mm, "mid": v(11.77, 38.49) * mm, "end": v(11.44, 38.34) * mm});
            skArc(sketch, "E12.34.5", {"start": v(12.62, 37.97) * mm, "mid": v(12.44, 38.28) * mm, "end": v(12.13, 38.47) * mm});
            skArc(sketch, "E12.34.6", {"start": v(13.02, 35.98) * mm, "mid": v(12.87, 36.98) * mm, "end": v(12.62, 37.97) * mm});
            skArc(sketch, "E12.34.7", {"start": v(12.97, 35.64) * mm, "mid": v(13.01, 35.8) * mm, "end": v(13.02, 35.98) * mm});
            skLineSegment(sketch, "E12.34.8", {"start": v(12.97, 35.64) * mm, "end": v(12.57, 34.55) * mm});
            skArc(sketch, "E12.34.9", {"start": v(12.57, 34.55) * mm, "mid": v(12.6, 33.95) * mm, "end": v(13.03, 33.54) * mm});
            skArc(sketch, "E12.35.0", {"start": v(2.36, 35.9) * mm, "mid": v(2.93, 36.1) * mm, "end": v(3.2, 36.62) * mm});
            skLineSegment(sketch, "E12.35.1", {"start": v(3.3, 37.78) * mm, "end": v(3.2, 36.62) * mm});
            skArc(sketch, "E12.35.2", {"start": v(3.4, 38.11) * mm, "mid": v(3.34, 37.95) * mm, "end": v(3.3, 37.78) * mm});
            skArc(sketch, "E12.35.3", {"start": v(3.4, 38.11) * mm, "mid": v(3.96, 38.96) * mm, "end": v(4.6, 39.75) * mm});
            skArc(sketch, "E12.35.4", {"start": v(5.27, 39.99) * mm, "mid": v(4.9, 39.95) * mm, "end": v(4.6, 39.75) * mm});
            skArc(sketch, "E12.35.5", {"start": v(5.84, 39.58) * mm, "mid": v(5.6, 39.86) * mm, "end": v(5.26, 39.99) * mm});
            skArc(sketch, "E12.35.6", {"start": v(6.57, 37.7) * mm, "mid": v(6.26, 38.66) * mm, "end": v(5.84, 39.58) * mm});
            skArc(sketch, "E12.35.7", {"start": v(6.59, 37.35) * mm, "mid": v(6.6, 37.52) * mm, "end": v(6.57, 37.7) * mm});
            skLineSegment(sketch, "E12.35.8", {"start": v(6.59, 37.35) * mm, "end": v(6.38, 36.2) * mm});
            skArc(sketch, "E12.35.9", {"start": v(6.38, 36.2) * mm, "mid": v(6.51, 35.62) * mm, "end": v(7.01, 35.29) * mm});
            skArc(sketch, "E13.trimOffspring", {"start": v(-35.9, 2.36) * mm, "mid": v(-35.94, 1.57) * mm, "end": v(-35.97, 0.78) * mm});
            skArc(sketch, "E14.trimOffspring", {"start": v(-35.77, -3.9) * mm, "mid": v(-35.67, -4.7) * mm, "end": v(-35.56, -5.48) * mm});
            skArc(sketch, "E15.trimOffspring", {"start": v(-34.95, 8.56) * mm, "mid": v(-35.13, 7.79) * mm, "end": v(-35.29, 7.01) * mm});
            skArc(sketch, "E16.trimOffspring", {"start": v(-34.54, -10.06) * mm, "mid": v(-34.31, -10.82) * mm, "end": v(-34.07, -11.57) * mm});
            skArc(sketch, "E17.trimOffspring", {"start": v(-32.27, -15.9) * mm, "mid": v(-31.91, -16.61) * mm, "end": v(-31.54, -17.31) * mm});
            skArc(sketch, "E18.trimOffspring", {"start": v(-29.02, -21.27) * mm, "mid": v(-28.54, -21.9) * mm, "end": v(-28.05, -22.53) * mm});
            skArc(sketch, "E19.trimOffspring", {"start": v(-24.89, -25.98) * mm, "mid": v(-24.3, -26.53) * mm, "end": v(-23.72, -27.06) * mm});
            skArc(sketch, "E20.trimOffspring", {"start": v(-20, -29.91) * mm, "mid": v(-19.33, -30.34) * mm, "end": v(-18.66, -30.76) * mm});
            skArc(sketch, "E21.trimOffspring", {"start": v(-14.5, -32.93) * mm, "mid": v(-13.77, -33.24) * mm, "end": v(-13.03, -33.54) * mm});
            skArc(sketch, "E22.trimOffspring", {"start": v(-8.56, -34.95) * mm, "mid": v(-7.79, -35.13) * mm, "end": v(-7.01, -35.29) * mm});
            skArc(sketch, "E23.trimOffspring", {"start": v(-2.36, -35.9) * mm, "mid": v(-1.57, -35.94) * mm, "end": v(-0.78, -35.97) * mm});
            skArc(sketch, "E24.trimOffspring", {"start": v(3.9, -35.77) * mm, "mid": v(4.7, -35.67) * mm, "end": v(5.48, -35.56) * mm});
            skArc(sketch, "E25.trimOffspring", {"start": v(10.06, -34.54) * mm, "mid": v(10.82, -34.31) * mm, "end": v(11.57, -34.07) * mm});
            skArc(sketch, "E26.trimOffspring", {"start": v(15.9, -32.27) * mm, "mid": v(16.61, -31.91) * mm, "end": v(17.31, -31.54) * mm});
            skArc(sketch, "E27.trimOffspring", {"start": v(21.27, -29.02) * mm, "mid": v(21.9, -28.54) * mm, "end": v(22.53, -28.05) * mm});
            skArc(sketch, "E28.trimOffspring", {"start": v(25.98, -24.89) * mm, "mid": v(26.53, -24.3) * mm, "end": v(27.06, -23.72) * mm});
            skArc(sketch, "E29.trimOffspring", {"start": v(29.91, -20) * mm, "mid": v(30.34, -19.33) * mm, "end": v(30.76, -18.66) * mm});
            skArc(sketch, "E30.trimOffspring", {"start": v(32.93, -14.5) * mm, "mid": v(33.24, -13.77) * mm, "end": v(33.54, -13.03) * mm});
            skArc(sketch, "E31.trimOffspring", {"start": v(34.95, -8.56) * mm, "mid": v(35.13, -7.79) * mm, "end": v(35.29, -7.01) * mm});
            skArc(sketch, "E32.trimOffspring", {"start": v(35.9, -2.36) * mm, "mid": v(35.94, -1.57) * mm, "end": v(35.97, -0.78) * mm});
            skArc(sketch, "E33.trimOffspring", {"start": v(35.77, 3.9) * mm, "mid": v(35.67, 4.7) * mm, "end": v(35.56, 5.48) * mm});
            skArc(sketch, "E34.trimOffspring", {"start": v(34.54, 10.06) * mm, "mid": v(34.31, 10.82) * mm, "end": v(34.07, 11.57) * mm});
            skArc(sketch, "E35.trimOffspring", {"start": v(32.27, 15.9) * mm, "mid": v(31.91, 16.61) * mm, "end": v(31.54, 17.31) * mm});
            skArc(sketch, "E36.trimOffspring", {"start": v(20, 29.91) * mm, "mid": v(19.33, 30.34) * mm, "end": v(18.66, 30.76) * mm});
            skArc(sketch, "E37.trimOffspring", {"start": v(29.02, 21.27) * mm, "mid": v(28.54, 21.9) * mm, "end": v(28.05, 22.53) * mm});
            skArc(sketch, "E38.trimOffspring", {"start": v(24.89, 25.98) * mm, "mid": v(24.3, 26.53) * mm, "end": v(23.72, 27.06) * mm});
            skArc(sketch, "E39.trimOffspring", {"start": v(14.5, 32.93) * mm, "mid": v(13.77, 33.24) * mm, "end": v(13.03, 33.54) * mm});
            skArc(sketch, "E40.trimOffspring", {"start": v(-25.98, 24.89) * mm, "mid": v(-26.53, 24.3) * mm, "end": v(-27.06, 23.72) * mm});
            skArc(sketch, "E41.trimOffspring", {"start": v(-32.93, 14.5) * mm, "mid": v(-33.24, 13.77) * mm, "end": v(-33.54, 13.03) * mm});
            skArc(sketch, "E42.trimOffspring", {"start": v(-29.91, 20) * mm, "mid": v(-30.34, 19.33) * mm, "end": v(-30.76, 18.66) * mm});
            skArc(sketch, "E43.trimOffspring", {"start": v(-21.27, 29.02) * mm, "mid": v(-21.9, 28.54) * mm, "end": v(-22.53, 28.05) * mm});
            skArc(sketch, "E44.trimOffspring", {"start": v(-15.9, 32.27) * mm, "mid": v(-16.61, 31.91) * mm, "end": v(-17.31, 31.54) * mm});
            skArc(sketch, "E45.trimOffspring", {"start": v(-10.06, 34.54) * mm, "mid": v(-10.82, 34.31) * mm, "end": v(-11.57, 34.07) * mm});
            skArc(sketch, "E46.trimOffspring", {"start": v(2.36, 35.9) * mm, "mid": v(1.57, 35.94) * mm, "end": v(0.78, 35.97) * mm});
            skArc(sketch, "E47.trimOffspring", {"start": v(8.56, 34.95) * mm, "mid": v(7.79, 35.13) * mm, "end": v(7.01, 35.29) * mm});
            skCircle(sketch, "E48", {"center": v(0, 0) * mm, "radius": 3.18 * mm});
            skSolve(sketch);
        }
        {
            var Q0;
            Q0=makeQuery(id+"F0.imprint","IMPRINT",FACE,{"disambiguationData":[TD([[makeQuery(id+"F0.imprint","IMPRINT",EDGE,{"derivedFrom":sQuery(id+"F0.wireOp",EDGE,"E0")}),1.0]])]});
            extrude(context, id + "F1", {"entities" : qUnion([Q0]), "depth" : 12.7 * mm});
        }
    });
